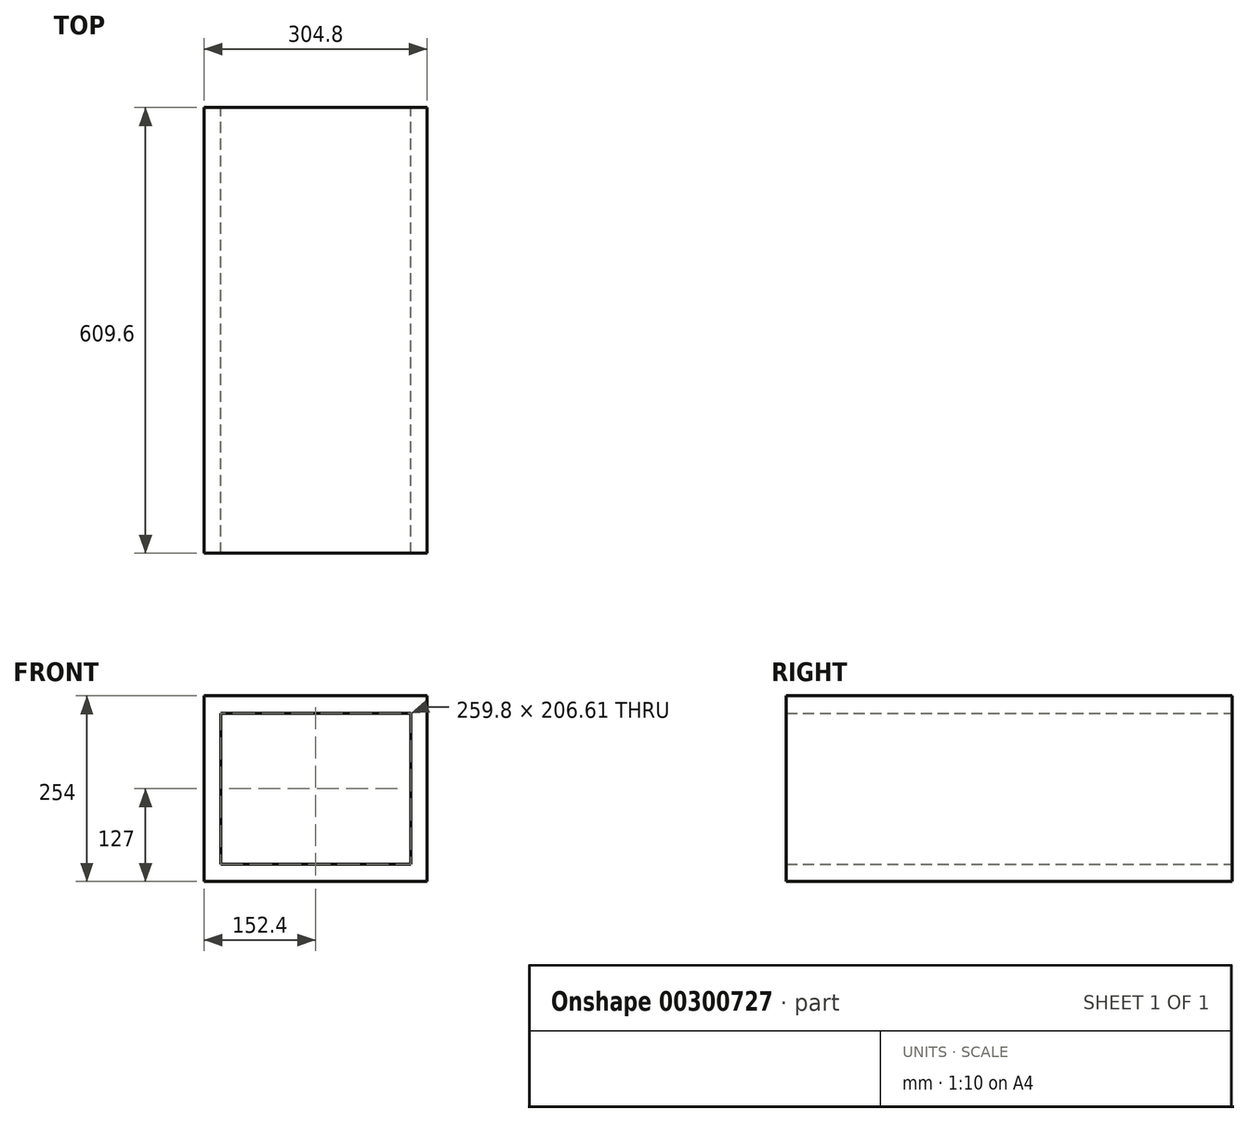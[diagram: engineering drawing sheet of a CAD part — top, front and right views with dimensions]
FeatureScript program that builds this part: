
annotation { "Feature Type Name" : "Feature", "Feature Type Description" : "" }
export const myFeature = defineFeature(function(context is Context, id is Id, definition is map)
    precondition{}
    {
        {
            var Q0;
            Q0=qCreatedBy(makeId("Front.planeOp"),FACE);
            var sketch = newSketch(context, id + "F0", { "sketchPlane" : qUnion([Q0])});
            skLineSegment(sketch, "E0.bottom", {"start": v(129.9, 103.3) * mm, "end": v(-129.9, 103.3) * mm});
            skLineSegment(sketch, "E0.top", {"start": v(129.9, -103.3) * mm, "end": v(-129.9, -103.3) * mm});
            skLineSegment(sketch, "E0.left", {"start": v(129.9, 103.3) * mm, "end": v(129.9, -103.3) * mm});
            skLineSegment(sketch, "E0.right", {"start": v(-129.9, 103.3) * mm, "end": v(-129.9, -103.3) * mm});
            skPoint(sketch, "E0.middle", {"position": v(0, 0) * mm});
            skLineSegment(sketch, "E1.bottom", {"start": v(152.4, 127) * mm, "end": v(-152.4, 127) * mm});
            skLineSegment(sketch, "E1.top", {"start": v(152.4, -127) * mm, "end": v(-152.4, -127) * mm});
            skLineSegment(sketch, "E1.left", {"start": v(152.4, 127) * mm, "end": v(152.4, -127) * mm});
            skLineSegment(sketch, "E1.right", {"start": v(-152.4, 127) * mm, "end": v(-152.4, -127) * mm});
            skSolve(sketch);
        }
        {
            var Q0;
            Q0 = qSketchRegion(id + "F0", true);
            extrude(context, id + "F1", {"entities" : qUnion([Q0]), "depth" : 609.6 * mm});
        }
        {
            var Q0;
            Q0=makeQuery(id+"F1.opExtrude","SWEPT_FACE",FACE,{"disambiguationData":[OSD([sQuery(id+"F0.wireOp",EDGE,"E1.left")])]});
            var sketch = newSketch(context, id + "F2", { "sketchPlane" : qUnion([Q0])});
            skLineSegment(sketch, "E2", {"start": v(-609.6, -127) * mm, "end": v(-331.16, 127) * mm});
            skSolve(sketch);
        }
        {
            var Q0;
            Q0=sQuery(id+"F2.wireOp",EDGE,"E2");
            extrude(context, id + "F3", {"bodyType" : ToolBodyType.SURFACE, "surfaceEntities" : qUnion([Q0]), "oppositeDirection" : true, "depth" : 317.5 * mm});
        }
    });
